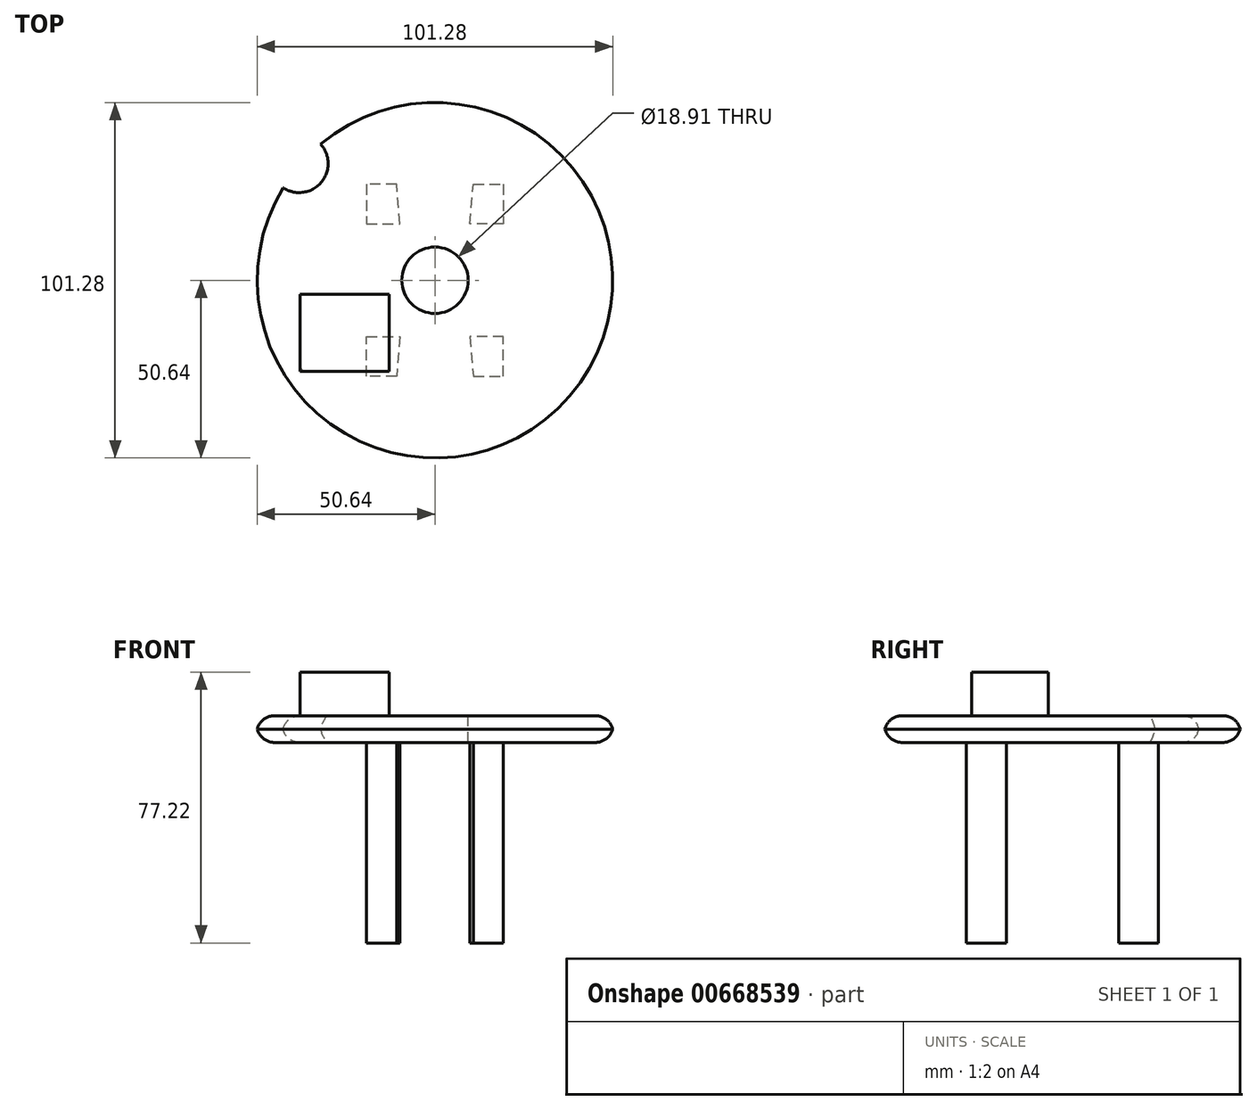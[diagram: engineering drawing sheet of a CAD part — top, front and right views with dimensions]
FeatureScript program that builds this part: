
annotation { "Feature Type Name" : "Feature", "Feature Type Description" : "" }
export const myFeature = defineFeature(function(context is Context, id is Id, definition is map)
    precondition{}
    {
        {
            var Q0;
            Q0=qCreatedBy(makeId("Top.planeOp"),FACE);
            var sketch = newSketch(context, id + "F0", { "sketchPlane" : qUnion([Q0])});
            skLineSegment(sketch, "E0", {"start": v(0, -50.8) * mm, "end": v(0, -50.8) * mm});
            skLineSegment(sketch, "E1", {"start": v(50.8, 0) * mm, "end": v(50.8, 0) * mm});
            skLineSegment(sketch, "E2", {"start": v(50.8, 0) * mm, "end": v(0, 0) * mm});
            skLineSegment(sketch, "E3", {"start": v(0, 0) * mm, "end": v(0, 0) * mm});
            skLineSegment(sketch, "E4", {"start": v(0, 0) * mm, "end": v(0, -50.8) * mm});
            skPoint(sketch, "E5.visualSharp", {"position": v(50.8, -50.8) * mm});
            skArc(sketch, "E5.filletArc", {"start": v(0, -50.8) * mm, "mid": v(35.92, -35.92) * mm, "end": v(50.8, 0) * mm});
            skSolve(sketch);
        }
        {
            var Q0;
            Q0=makeQuery(id+"F0.imprint","IMPRINT",FACE,{"disambiguationData":[TD([[makeQuery(id+"F0.imprint","IMPRINT",EDGE,{"derivedFrom":sQuery(id+"F0.wireOp",EDGE,"E2")}),1.0]])]});
            extrude(context, id + "F1", {"entities" : qUnion([Q0]), "depth" : 7.62 * mm, "offsetDistance" : 25.4 * mm});
        }
        {
            var Q0;
            Q0=makeQuery(id+"F1.opExtrude","CAP_FACE",FACE,{"disambiguationData":[OSD([sQuery(id+"F0.wireOp",EDGE,"E2"),sQuery(id+"F0.wireOp",EDGE,"E4"),sQuery(id+"F0.wireOp",EDGE,"E5.filletArc")])],"isStart":true});
            var sketch = newSketch(context, id + "F2", { "sketchPlane" : qUnion([Q0])});
            skLineSegment(sketch, "E6", {"start": v(10.95, 27.37) * mm, "end": v(19.5, 27.37) * mm});
            skLineSegment(sketch, "E7", {"start": v(19.5, 27.37) * mm, "end": v(19.5, 16.02) * mm});
            skLineSegment(sketch, "E8", {"start": v(19.5, 16.02) * mm, "end": v(9.95, 16.02) * mm});
            skLineSegment(sketch, "E9", {"start": v(9.95, 16.02) * mm, "end": v(10.95, 27.37) * mm});
            skSolve(sketch);
        }
        {
            var Q0;
            Q0 = qSketchRegion(id + "F2", true);
            extrude(context, id + "F3", {"entities" : qUnion([Q0]), "operationType" : NewBodyOperationType.ADD, "depth" : 57.15 * mm, "offsetDistance" : 25.4 * mm});
        }
        {
            var Q0;
            Q0=makeQuery(id+"F1.opExtrude","CAP_EDGE",EDGE,{"disambiguationData":[OSD([sQuery(id+"F0.wireOp",EDGE,"E5.filletArc")])],"isStart":false});
            var Q1;
            Q1=makeQuery(id+"F1.opExtrude","CAP_EDGE",EDGE,{"disambiguationData":[OSD([sQuery(id+"F0.wireOp",EDGE,"E5.filletArc")])],"isStart":true});
            fillet(context, id + "F4", {"entities" : qUnion([Q0, Q1]), "radius" : 5.08 * mm, "tangentPropagation" : true, "allowEdgeOverflow" : false});
        }
        {
            var Q0;
            Q0=makeQuery(id+"F1.opExtrude","SWEPT_BODY",BODY,{"disambiguationData":[OSD([sQuery(id+"F0.wireOp",EDGE,"E2"),sQuery(id+"F0.wireOp",EDGE,"E4"),sQuery(id+"F0.wireOp",EDGE,"E5.filletArc")])]});
            var Q1;
            Q1=qCreatedBy(makeId("Right.planeOp"),FACE);
            mirror(context, id + "F5", {"operationType" : NewBodyOperationType.ADD, "entities" : qUnion([Q0]), "mirrorPlane" : qUnion([Q1])});
        }
        {
            var Q0;
            Q0=makeQuery(id+"F1.opExtrude","SWEPT_BODY",BODY,{"disambiguationData":[OSD([sQuery(id+"F0.wireOp",EDGE,"E2"),sQuery(id+"F0.wireOp",EDGE,"E4"),sQuery(id+"F0.wireOp",EDGE,"E5.filletArc")])]});
            var Q1;
            Q1=qCreatedBy(makeId("Front.planeOp"),FACE);
            mirror(context, id + "F6", {"operationType" : NewBodyOperationType.ADD, "entities" : qUnion([Q0]), "mirrorPlane" : qUnion([Q1])});
        }
        {
            var Q0;
            {var subQ0=makeQuery(id+"F1.opExtrude","CAP_FACE",FACE,{"disambiguationData":[OSD([sQuery(id+"F0.wireOp",EDGE,"E2"),sQuery(id+"F0.wireOp",EDGE,"E4"),sQuery(id+"F0.wireOp",EDGE,"E5.filletArc")])],"isStart":false});var subQ1=makeQuery(id+"F5.boolean.opBoolean","MERGE",FACE,{"derivedFrom":[subQ0,makeQuery(id+"F5.opPattern","COPY",FACE,{"derivedFrom":subQ0,"instanceName":"1"})]});Q0=makeQuery(id+"F6.boolean.opBoolean","MERGE",FACE,{"derivedFrom":[subQ1,makeQuery(id+"F6.opPattern","COPY",FACE,{"derivedFrom":subQ1,"instanceName":"1"})]});}
            var sketch = newSketch(context, id + "F7", { "sketchPlane" : qUnion([Q0])});
            skCircle(sketch, "E10", {"center": v(-38.7, 33.23) * mm, "radius": 8.25 * mm});
            skSolve(sketch);
        }
        {
            var Q0;
            Q0 = qSketchRegion(id + "F7", true);
            extrude(context, id + "F8", {"entities" : qUnion([Q0]), "operationType" : NewBodyOperationType.REMOVE, "oppositeDirection" : true, "depth" : 25.4 * mm, "offsetDistance" : 25.4 * mm});
        }
        {
            var Q0;
            {var subQ0=makeQuery(id+"F1.opExtrude","CAP_FACE",FACE,{"disambiguationData":[OSD([sQuery(id+"F0.wireOp",EDGE,"E2"),sQuery(id+"F0.wireOp",EDGE,"E4"),sQuery(id+"F0.wireOp",EDGE,"E5.filletArc")])],"isStart":false});var subQ1=makeQuery(id+"F5.boolean.opBoolean","MERGE",FACE,{"derivedFrom":[subQ0,makeQuery(id+"F5.opPattern","COPY",FACE,{"derivedFrom":subQ0,"instanceName":"1"})]});Q0=makeQuery(id+"F6.boolean.opBoolean","MERGE",FACE,{"derivedFrom":[subQ1,makeQuery(id+"F6.opPattern","COPY",FACE,{"derivedFrom":subQ1,"instanceName":"1"})]});}
            var sketch = newSketch(context, id + "F9", { "sketchPlane" : qUnion([Q0])});
            skCircle(sketch, "E11", {"center": v(0, 0) * mm, "radius": 9.45 * mm});
            skSolve(sketch);
        }
        {
            var Q0;
            Q0 = qSketchRegion(id + "F9", true);
            extrude(context, id + "F10", {"entities" : qUnion([Q0]), "operationType" : NewBodyOperationType.REMOVE, "oppositeDirection" : true, "depth" : 26.16 * mm, "offsetDistance" : 25.4 * mm});
        }
        {
            var Q0;
            {var subQ0=makeQuery(id+"F1.opExtrude","CAP_FACE",FACE,{"disambiguationData":[OSD([sQuery(id+"F0.wireOp",EDGE,"E2"),sQuery(id+"F0.wireOp",EDGE,"E4"),sQuery(id+"F0.wireOp",EDGE,"E5.filletArc")])],"isStart":false});var subQ1=makeQuery(id+"F5.boolean.opBoolean","MERGE",FACE,{"derivedFrom":[subQ0,makeQuery(id+"F5.opPattern","COPY",FACE,{"derivedFrom":subQ0,"instanceName":"1"})]});Q0=makeQuery(id+"F6.boolean.opBoolean","MERGE",FACE,{"derivedFrom":[subQ1,makeQuery(id+"F6.opPattern","COPY",FACE,{"derivedFrom":subQ1,"instanceName":"1"})]});}
            var sketch = newSketch(context, id + "F11", { "sketchPlane" : qUnion([Q0])});
            skLineSegment(sketch, "E12.bottom", {"start": v(-38.4, -4.05) * mm, "end": v(-13, -4.05) * mm});
            skLineSegment(sketch, "E12.top", {"start": v(-38.4, -25.9) * mm, "end": v(-13, -25.9) * mm});
            skLineSegment(sketch, "E12.left", {"start": v(-38.4, -4.05) * mm, "end": v(-38.4, -25.9) * mm});
            skLineSegment(sketch, "E12.right", {"start": v(-13, -4.05) * mm, "end": v(-13, -25.9) * mm});
            skSolve(sketch);
        }
        {
            var Q0;
            Q0 = qSketchRegion(id + "F11", true);
            extrude(context, id + "F12", {"entities" : qUnion([Q0]), "operationType" : NewBodyOperationType.ADD, "depth" : 12.45 * mm, "offsetDistance" : 25.4 * mm});
        }
    });
